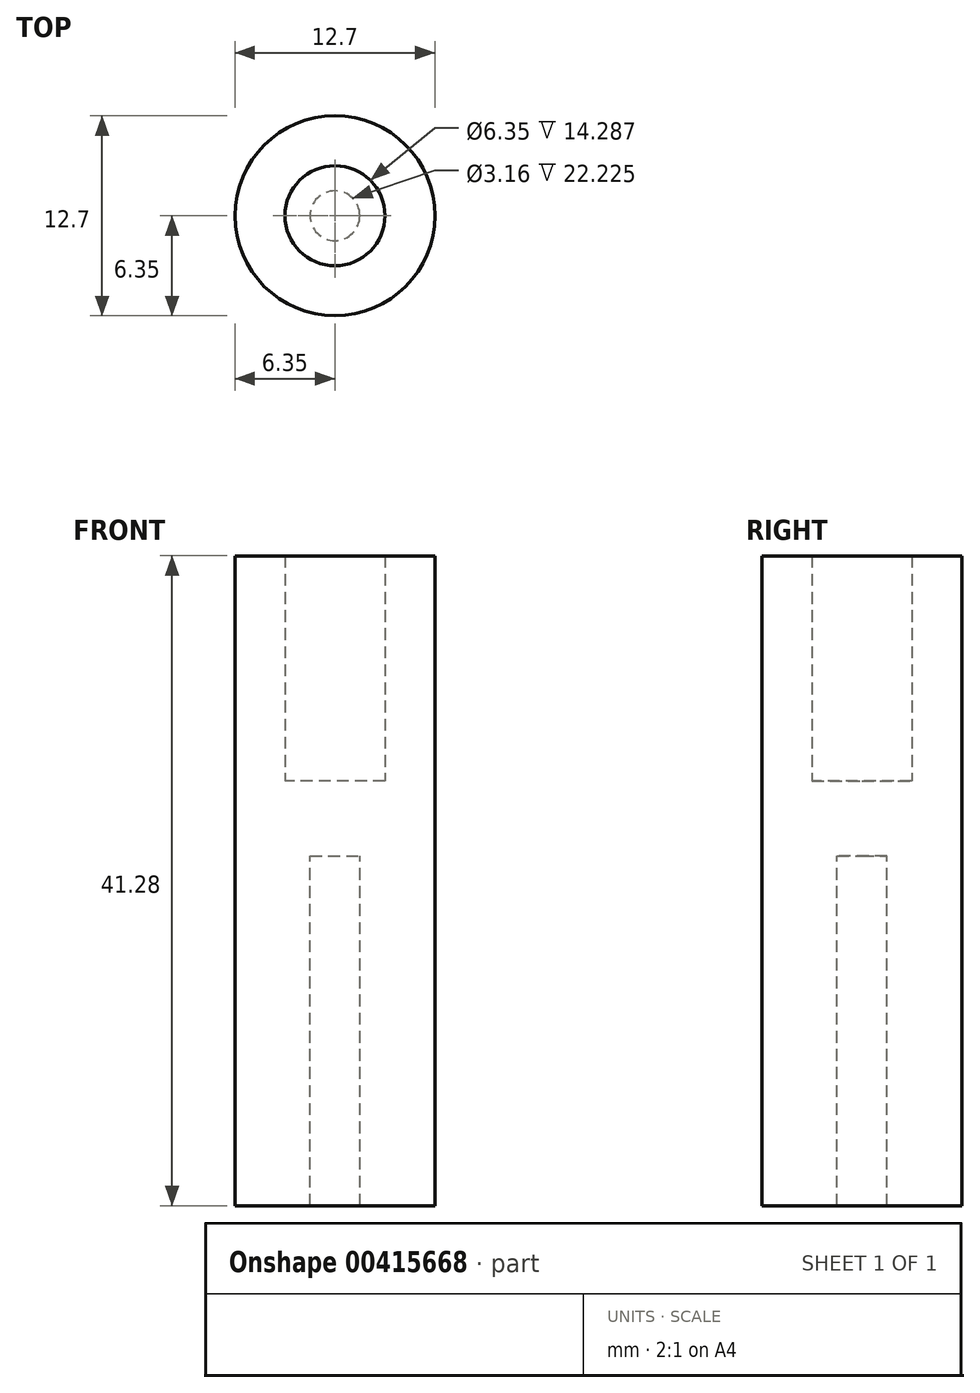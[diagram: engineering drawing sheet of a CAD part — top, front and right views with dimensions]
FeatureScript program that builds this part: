
annotation { "Feature Type Name" : "Feature", "Feature Type Description" : "" }
export const myFeature = defineFeature(function(context is Context, id is Id, definition is map)
    precondition{}
    {
        {
            var Q0;
            Q0=qCreatedBy(makeId("Top.planeOp"),FACE);
            var sketch = newSketch(context, id + "F0", { "sketchPlane" : qUnion([Q0])});
            skCircle(sketch, "E0", {"center": v(0, 0) * mm, "radius": 6.35 * mm});
            skCircle(sketch, "E1", {"center": v(0, 0) * mm, "radius": 3.18 * mm});
            skSolve(sketch);
        }
        {
            var Q0;
            Q0=makeQuery(id+"F0.imprint","IMPRINT",FACE,{"disambiguationData":[TD([[makeQuery(id+"F0.imprint","IMPRINT",EDGE,{"derivedFrom":sQuery(id+"F0.wireOp",EDGE,"E0")}),1.0]])]});
            extrude(context, id + "F1", {"entities" : qUnion([Q0]), "depth" : 14.29 * mm});
        }
        {
            var Q0;
            Q0=makeQuery(id+"F0.imprint","IMPRINT",FACE,{"disambiguationData":[TD([[makeQuery(id+"F0.imprint","IMPRINT",EDGE,{"derivedFrom":sQuery(id+"F0.wireOp",EDGE,"E0")}),1.0]])]});
            var sketch = newSketch(context, id + "F2", { "sketchPlane" : qUnion([Q0])});
            skCircle(sketch, "E2", {"center": v(0, 0) * mm, "radius": 6.35 * mm});
            skSolve(sketch);
        }
        {
            var Q0;
            Q0=qSketchRegion(id+"F2",true);
            extrude(context, id + "F3", {"entities" : qUnion([Q0]), "operationType" : NewBodyOperationType.ADD, "oppositeDirection" : true, "depth" : 4.76 * mm});
        }
        {
            var Q0;
            Q0=makeQuery(id+"F3.opExtrude","CAP_FACE",FACE,{"disambiguationData":[OSD([sQuery(id+"F2.wireOp",EDGE,"E2")])],"isStart":false});
            var sketch = newSketch(context, id + "F4", { "sketchPlane" : qUnion([Q0])});
            skPoint(sketch, "E3.middle", {"position": v(0, 0) * mm});
            skCircle(sketch, "E4", {"center": v(0, 0) * mm, "radius": 1.58 * mm});
            skSolve(sketch);
        }
        {
            var Q0;
            Q0=makeQuery(id+"F4.imprint","IMPRINT",FACE,{"disambiguationData":[TD([[makeQuery(id+"F4.imprint","IMPRINT",EDGE,{"derivedFrom":sQuery(id+"F4.wireOp",EDGE,"E4")}),-1.0]])]});
            extrude(context, id + "F5", {"entities" : qUnion([Q0]), "operationType" : NewBodyOperationType.ADD, "depth" : 22.22 * mm});
        }
    });
